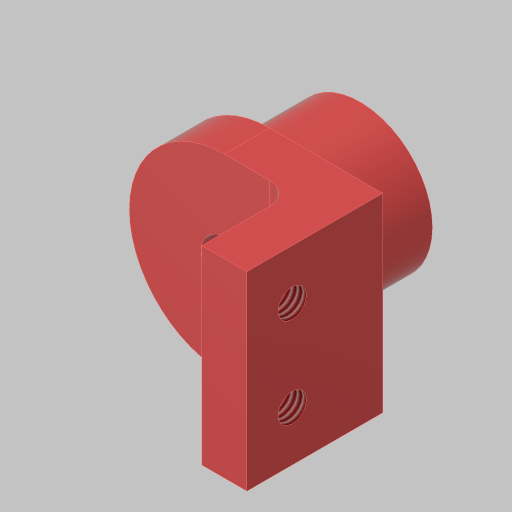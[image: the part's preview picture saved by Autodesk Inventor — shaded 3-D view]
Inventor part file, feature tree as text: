
AUTODESK INVENTOR PART (.ipt)
format: ipt  version: 2023.5 (Build 275446000, 446)  size: 154,112 bytes
history: native  units: in
note: dims shown in document units (in); Inventor stores cm internally (conversion verified against a paired STEP export)
features: sketch x5, extrude x3, hole x2, fillet x1, projected_geometry x1
ambient origin geometry x8: Origin, YZ Plane, XZ Plane, XY Plane, X Axis, Y Axis, Z Axis, Center Point
bodies: Solid1 (feature_tree)
feature tree (12):
  extrude  "Extrusion1"  Depth=0.5in TaperAngle=0.0deg
  extrude  "Extrusion2"  Depth=0.25in TaperAngle=0.0deg
  hole  "Hole2"  [1 undecoded]
  extrude  "Extrusion3"  Depth=0.25in
  fillet  "Fillet1"  Radius=0.5in
  hole  "Hole3"  [1 undecoded]
  sketch  "Sketch1"  dims[d0=0.8in d1=0.5in d2=0.0in]
  sketch  "Sketch2"  dims[d3=0.125in d4=0.25in d5=0.0in]
  sketch  "Sketch4"  dims[d6=0.688in d14=0.625in]
  sketch  "Sketch5"  dims[d15=0.257in d16=0.75in d17=0.375in d18=0.25in d19=0.5635in d20=1.0in d21=0.8108in d22=0.25in d23=0.5in d24=0.0in]
  sketch  "Sketch6"  dims[d25=0.125in d26=0.5in d27=0.156in d28=0.38in d29=0.385in d30=0.25in d31=0.5635in d32=1.0in d33=0.8108in d34=0.25in]
  projected_geometry  "Project Cut Edges1"
note: 2 required parameter values undecoded (feature->parameter linkage not recoverable at this tier; creation-order binding heuristic only, values carry confidence <= 0.55)
